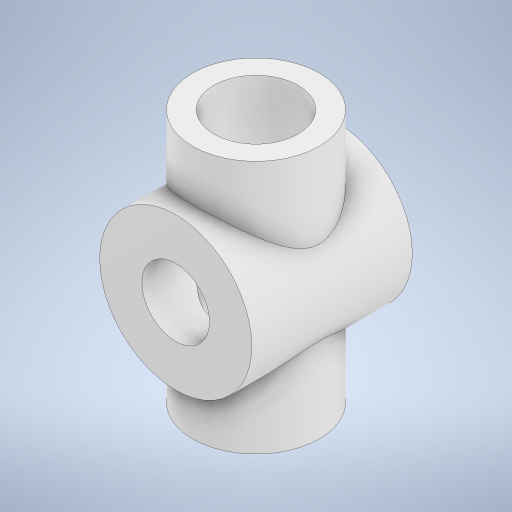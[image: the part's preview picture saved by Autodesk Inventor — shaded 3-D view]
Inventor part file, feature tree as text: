
AUTODESK INVENTOR PART (.ipt)
format: ipt  version: 2023 (Build 270158030, 158C)  size: 326,144 bytes
history: native  units: in
note: dims shown in document units (in); Inventor stores cm internally (conversion verified against a paired STEP export)
features: sketch x6, extrude x4, plane x1, revolve x1, mirror x1, hole x1
ambient origin geometry x8: Origin, YZ Plane, XZ Plane, XY Plane, X Axis, Y Axis, Z Axis, Center Point
bodies: Solid1 (feature_tree)
feature tree (14):
  extrude  "Extrusion1"  Depth=0.3937in
  plane  "Work Plane2"
  extrude  "Extrusion3"  Depth=0.5512in
  revolve  "Revolution1"  [1 undecoded]
  mirror  "Mirror3"
  extrude  "Extrusion4"  TaperAngle=360.0deg  [1 undecoded]
  hole  "Hole4"  [1 undecoded]
  extrude  "Extrusion5"  TaperAngle=0.0deg  [1 undecoded]
  sketch  "Sketch1"  dims[d3=1.1811in d4=0.0in d37=0.3937in]
  sketch  "Sketch7"  dims[d38=0.5906in d39=0.5512in]
  sketch  "Sketch8"  dims[d40=0.0787in d41=0.0591in d42=0.0in d43=0.0in d44=0.5512in]
  sketch  "Sketch9"  dims[d46=0.0787in d47=360.0deg]
  sketch  "Sketch10"  dims[d48=0.0in d49=0.0in d50=0.1575in]
  sketch  "Sketch11"  dims[d51=0.315in d52=0.2362in d53=0.1575in d54=0.0787in d55=90.0deg d56=0.315in d57=0.8108in d58=0.0in d59=0.0in]
note: 4 required parameter values undecoded (feature->parameter linkage not recoverable at this tier; creation-order binding heuristic only, values carry confidence <= 0.55)